# Revit family: Brushed Stainless Steel #4
name_source: partatom
category: Specialty Equipment
units: mm (PartAtom-declared; Revit-internal decimal feet)

## family parameters
Always vertical = Yes
Cut with Voids When Loaded = No
OmniClass Number = 23.40.40.14.24.14
OmniClass Title = Service Line Equipment
Part Type = Normal
Room Calculation Point = No
Round Connector Dimension = Use Diameter
Shared = No
Work Plane-Based = Yes

## types (1)
- Brushed Stainless Steel #4
    Assembly Code = E1090320
    CSI MasterFormat = 11 46 16
    Default Elevation = 4' - 0"
    Depth = 1' - 8 1/2"
    Description = Food Shield
    Foodservice Equipment Identifier = Yes
    Frame Material = QF_Stainless-Brushed-Satin
    Height = 1' - 8 5/16"
    Identify Quantity as Lot = Yes
    KCL SpecSheet URL = http://kclweb.kclcad.com
    KCLRef = KCL2C9,,3e3dc4d2-6e05-4f15-88d2-2f3e74d89ae3,PB,TMIR-G,638126355580000000,54b9e17d-0049-4681-9c17-c7353eb1b90e,a09dcd36-3c19-41af-8594-96333e29a47a
    Manufacturer = Premier Metal And Glass
    Masterspec = Division 11
    Model = TMIR-G
    Specification by Manufacturer = 1Guard™ Fixed Self-Service Sneeze Guard, double sided guard with top shelf, slanted front, tempered glass with
polished edges, end panels, 1" OD round stainless supports, NSF (Contact Premier Sales Department for Pricing)
    URL = https://www.pmg-inc.com
    URL Cutsheet = https://www.pmg-inc.me
    Weight in Pounds = 0

## geometry (parser evidence)
native form markers: Sweep x58
no freeform markers — native parametric forms only
